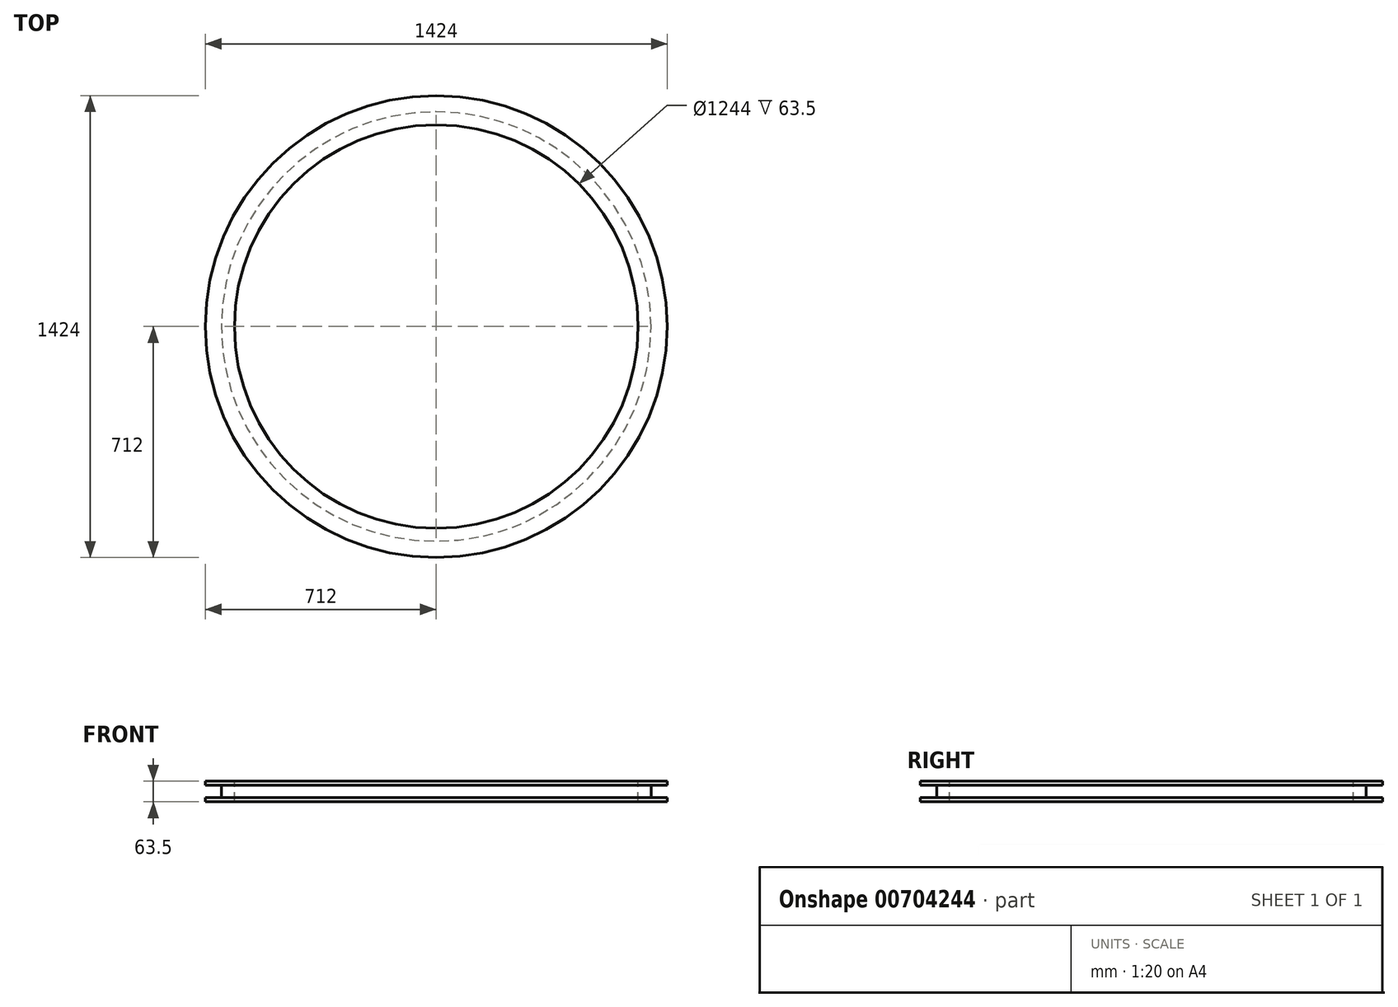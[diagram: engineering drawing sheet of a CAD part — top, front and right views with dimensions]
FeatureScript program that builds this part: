
annotation { "Feature Type Name" : "Feature", "Feature Type Description" : "" }
export const myFeature = defineFeature(function(context is Context, id is Id, definition is map)
    precondition{}
    {
        {
            var Q0;
            Q0=qCreatedBy(makeId("Front.planeOp"),FACE);
            var sketch = newSketch(context, id + "F0", { "sketchPlane" : qUnion([Q0])});
            skLineSegment(sketch, "E0.bottom", {"start": v(0, 63.5) * mm, "end": v(-622, 63.5) * mm});
            skLineSegment(sketch, "E0.top", {"start": v(0, 0) * mm, "end": v(-622, 0) * mm});
            skLineSegment(sketch, "E0.left", {"start": v(0, 63.5) * mm, "end": v(0, 0) * mm});
            skLineSegment(sketch, "E0.right", {"start": v(-622, 63.5) * mm, "end": v(-622, 0) * mm});
            skLineSegment(sketch, "E1.bottom", {"start": v(-622, 63.5) * mm, "end": v(-662, 63.5) * mm});
            skLineSegment(sketch, "E1.top", {"start": v(-622, 0) * mm, "end": v(-662, 0) * mm});
            skLineSegment(sketch, "E1.right", {"start": v(-662, 63.5) * mm, "end": v(-662, 0) * mm});
            skLineSegment(sketch, "E2.bottom", {"start": v(-662, 63.5) * mm, "end": v(-712, 63.5) * mm});
            skLineSegment(sketch, "E2.top", {"start": v(-662, 50.8) * mm, "end": v(-712, 50.8) * mm});
            skLineSegment(sketch, "E2.left", {"start": v(-662, 63.5) * mm, "end": v(-662, 50.8) * mm});
            skLineSegment(sketch, "E2.right", {"start": v(-712, 63.5) * mm, "end": v(-712, 50.8) * mm});
            skLineSegment(sketch, "E3.bottom", {"start": v(-662, 0) * mm, "end": v(-712, 0) * mm});
            skLineSegment(sketch, "E3.top", {"start": v(-662, 12.7) * mm, "end": v(-712, 12.7) * mm});
            skLineSegment(sketch, "E3.left", {"start": v(-662, 0) * mm, "end": v(-662, 12.7) * mm});
            skLineSegment(sketch, "E3.right", {"start": v(-712, 0) * mm, "end": v(-712, 12.7) * mm});
            skLineSegment(sketch, "E4.bottom", {"start": v(-712, 12.7) * mm, "end": v(-672, 12.7) * mm});
            skLineSegment(sketch, "E4.top", {"start": v(-712, 25.4) * mm, "end": v(-672, 25.4) * mm});
            skLineSegment(sketch, "E4.left", {"start": v(-712, 12.7) * mm, "end": v(-712, 25.4) * mm});
            skLineSegment(sketch, "E4.right", {"start": v(-672, 12.7) * mm, "end": v(-672, 25.4) * mm});
            skLineSegment(sketch, "E5.bottom", {"start": v(-712, 50.8) * mm, "end": v(-672, 50.8) * mm});
            skLineSegment(sketch, "E5.top", {"start": v(-712, 38.1) * mm, "end": v(-672, 38.1) * mm});
            skLineSegment(sketch, "E5.left", {"start": v(-712, 50.8) * mm, "end": v(-712, 38.1) * mm});
            skLineSegment(sketch, "E5.right", {"start": v(-672, 50.8) * mm, "end": v(-672, 38.1) * mm});
            skLineSegment(sketch, "E6.bottom", {"start": v(0, 63.5) * mm, "end": v(622, 63.5) * mm});
            skLineSegment(sketch, "E6.top", {"start": v(0, 0) * mm, "end": v(622, 0) * mm});
            skLineSegment(sketch, "E6.right", {"start": v(622, 63.5) * mm, "end": v(622, 0) * mm});
            skSolve(sketch);
        }
        {
            var Q0;
            Q0=makeQuery(id+"F0.imprint","IMPRINT",FACE,{"disambiguationData":[TD([[makeQuery(id+"F0.imprint","IMPRINT",EDGE,{"derivedFrom":sQuery(id+"F0.wireOp",EDGE,"E1.bottom")}),1.0]])]});
            var Q1;
            Q1=sQuery(id+"F0.wireOp",EDGE,"E0.left");
            revolve(context, id + "F1", {"surfaceOperationType" : NewSurfaceOperationType.NEW, "entities" : qUnion([Q0]), "axis" : qUnion([Q1]), "revolveType" : RevolveType.FULL});
        }
        {
            var Q0;
            Q0=makeQuery(id+"F0.imprint","IMPRINT",FACE,{"disambiguationData":[TD([[makeQuery(id+"F0.imprint","IMPRINT",EDGE,{"derivedFrom":sQuery(id+"F0.wireOp",EDGE,"E2.bottom")}),1.0]])]});
            var Q1;
            Q1=makeQuery(id+"F0.imprint","IMPRINT",FACE,{"disambiguationData":[TD([[makeQuery(id+"F0.imprint","IMPRINT",EDGE,{"derivedFrom":sQuery(id+"F0.wireOp",EDGE,"E5.bottom")}),-1.0]])]});
            var Q2;
            Q2=sQuery(id+"F0.wireOp",EDGE,"E0.left");
            revolve(context, id + "F2", {"operationType" : NewBodyOperationType.ADD, "surfaceOperationType" : NewSurfaceOperationType.NEW, "entities" : qUnion([Q0, Q1]), "axis" : qUnion([Q2]), "revolveType" : RevolveType.FULL});
        }
        {
            var Q0;
            Q0=makeQuery(id+"F0.imprint","IMPRINT",FACE,{"disambiguationData":[TD([[makeQuery(id+"F0.imprint","IMPRINT",EDGE,{"derivedFrom":sQuery(id+"F0.wireOp",EDGE,"E4.bottom")}),1.0]])]});
            var Q1;
            Q1=makeQuery(id+"F0.imprint","IMPRINT",FACE,{"disambiguationData":[TD([[makeQuery(id+"F0.imprint","IMPRINT",EDGE,{"derivedFrom":sQuery(id+"F0.wireOp",EDGE,"E3.bottom")}),-1.0]])]});
            var Q2;
            Q2=sQuery(id+"F0.wireOp",EDGE,"E0.left");
            revolve(context, id + "F3", {"operationType" : NewBodyOperationType.ADD, "surfaceOperationType" : NewSurfaceOperationType.NEW, "entities" : qUnion([Q0, Q1]), "axis" : qUnion([Q2]), "revolveType" : RevolveType.FULL});
        }
    });
